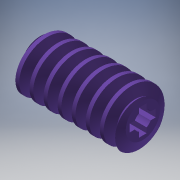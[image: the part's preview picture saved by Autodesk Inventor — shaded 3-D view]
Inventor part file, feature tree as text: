
AUTODESK INVENTOR PART (.ipt)
format: ipt  version: 2019.3 (Build 233278000, 278)  size: 406,528 bytes
history: native  units: mm (DEFAULTED — no unit token found)
features: other x6, extrude x3, sketch x3, chamfer x2, pattern_circular x2
ambient origin geometry x6: Origin, XZ Plane, X Axis, Y Axis, Z Axis, Center Point
bodies: Solid1 (feature_tree)
feature tree (16):
  extrude  "Base Body"  Depth=19.404171mm
  chamfer  "Chamfer1"  Distance=1.294799mm
  chamfer  "Chamfer2"  Distance=3.557431mm
  other  "Tooth Sketch"
  other  "Left Tooth"
  pattern_circular  "Left Tooth Pattern"  [2 undecoded]
  other  "Tooth"
  pattern_circular  "Tooth Pattern"  [2 undecoded]
  extrude  "Extrusion2"  Depth=10.0mm
  extrude  "Extrusion3"  Depth=10.0mm
  other  "Base Body Sketch"
  sketch  "Sketch5"  dims[d4=40.0mm d5=19.404171mm]
  other  "Srf1"
  sketch  "Sketch6"  dims[d6=38.1mm]
  sketch  "Sketch9"  dims[d7=0.0mm d8=1.294799mm d9=3.557431mm d10=1.294799mm d11=3.557431mm d12=19.198622mm d14=3.1425mm d24=19.198622mm d25=22.86mm d26=1.27mm d27=6.144654mm d28=8.085071mm d29=9.799106mm d30=5.08mm d31=10.0mm d32=100.0mm d33=0.0mm d34=90.0deg d35=90.0deg d36=0.0mm d37=0.0mm d43=10.0mm d45=360.0deg d46=45.0deg d47=45.0deg d49=0.0mm d53=0.0mm d54=48.510427mm d55=0.0mm d56=0.0mm d57=16.170142mm d58=25.4mm d59=0.0mm d60=5.08mm d61=25.4mm d62=100.0mm d63=0.0mm d64=90.0deg d65=90.0deg d66=0.0mm d67=0.0mm d68=10.0mm d69=10.0mm d70=360.0deg d72=10.0mm d74=10.0mm d75=10.0mm d76=0.0mm d77=48.510427mm d78=6.35mm d79=25.4mm d80=0.0mm d95=1.397mm d96=4.699mm d97=40.0mm d99=360.0deg d101=25.4mm d102=0.0mm]
  other  "Pitch Diameter"
note: 4 required parameter values undecoded (feature->parameter linkage not recoverable at this tier; creation-order binding heuristic only, values carry confidence <= 0.55)
